# Revit family: TPU5300DA1I-WS
name_source: partatom
category: Оборудование
revit_build: Autodesk Revit 2018 (Build: 20180423_1000(x64)
units: mm (PartAtom-declared; Revit-internal decimal feet)

## family parameters
Всегда вертикально = Да
Классификация = Нет
На основе рабочей плоскости = Нет
Общий = Нет
При загрузке вырезать с полостями = Нет
Размер круглого соединителя = Использовать диаметр
Тип детали = Нормальный
Точка расчета площади = Нет

## types (1)
- TPU5300DA1I-WS
    Air Outlet (H) = 110 мм
    Air Outlet (L) = 832 мм
    Air Return (H) = 172 мм
    Air Return (L) = 977 мм
    Вес блока, кг = 20
    Высота = 200 мм
    Глубина = 470 мм
    Группа модели = Перманентный агрегат
    Диаметр газовой трубы, мм (дюймы) = 12,70 (1/2)
    Диаметр дренажной трубы, мм = 20
    Диаметр жидкостной трубы, мм (дюймы) = 6,35 (1/4)
    Изготовитель = TIZEST
    Описание = Внутренний блок
    Производительность (охл.), кВт = 5.3
    Размеры блока (ВхШхГ), мм = 1000×500×200
    Ширина = 1000 мм
